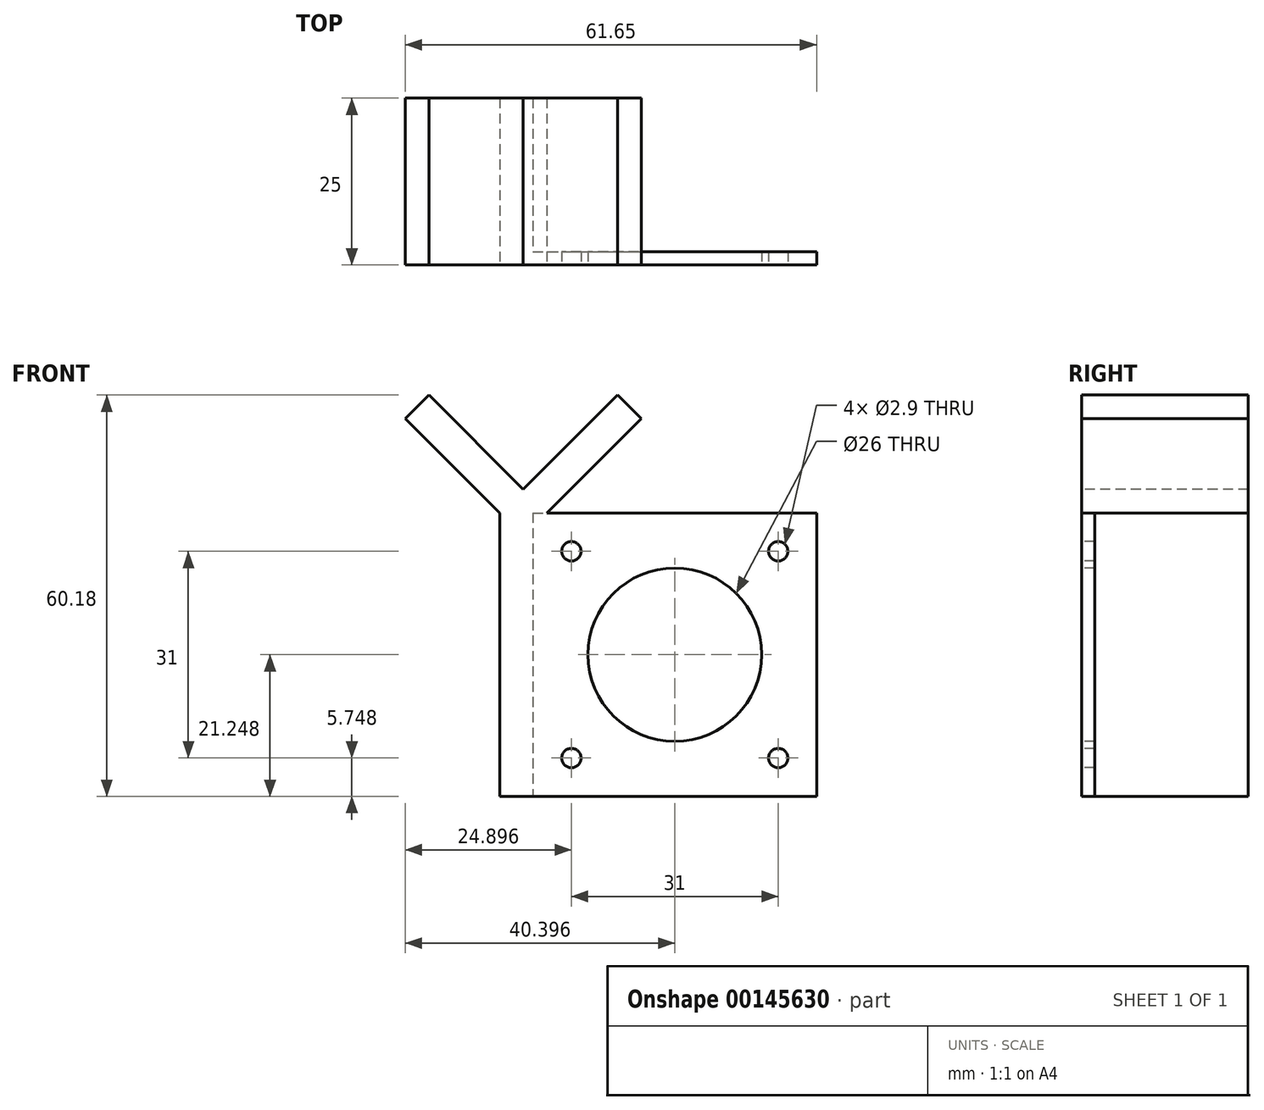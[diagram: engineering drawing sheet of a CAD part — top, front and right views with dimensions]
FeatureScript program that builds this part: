
annotation { "Feature Type Name" : "Feature", "Feature Type Description" : "" }
export const myFeature = defineFeature(function(context is Context, id is Id, definition is map)
    precondition{}
    {
        {
            var Q0;
            Q0=qCreatedBy(makeId("Front.planeOp"),FACE);
            var sketch = newSketch(context, id + "F0", { "sketchPlane" : qUnion([Q0])});
            skLineSegment(sketch, "E0.bottom", {"start": v(-36.86, -9.24) * mm, "end": v(-31.86, -9.24) * mm});
            skLineSegment(sketch, "E0.top", {"start": v(-36.86, -51.74) * mm, "end": v(-31.86, -51.74) * mm});
            skLineSegment(sketch, "E0.left", {"start": v(-36.86, -9.24) * mm, "end": v(-36.86, -51.74) * mm});
            skLineSegment(sketch, "E1.bottom", {"start": v(-31.86, -9.24) * mm, "end": v(10.64, -9.24) * mm});
            skLineSegment(sketch, "E1.top", {"start": v(-31.86, -51.74) * mm, "end": v(10.64, -51.74) * mm});
            skLineSegment(sketch, "E1.left", {"start": v(-31.86, -9.24) * mm, "end": v(-31.86, -51.74) * mm});
            skLineSegment(sketch, "E1.right", {"start": v(10.64, -9.24) * mm, "end": v(10.64, -51.74) * mm});
            skCircle(sketch, "E2", {"center": v(-26.11, -15) * mm, "radius": 1.45 * mm});
            skCircle(sketch, "E3", {"center": v(4.89, -15) * mm, "radius": 1.45 * mm});
            skCircle(sketch, "E4", {"center": v(-26.11, -46) * mm, "radius": 1.45 * mm});
            skCircle(sketch, "E5", {"center": v(4.89, -46) * mm, "radius": 1.45 * mm});
            skLineSegment(sketch, "E6", {"start": v(-29.8, -9.24) * mm, "end": v(-15.65, 4.9) * mm});
            skCircle(sketch, "E7", {"center": v(-10.61, -30.5) * mm, "radius": 13 * mm});
            skLineSegment(sketch, "E8", {"start": v(-47.47, 8.44) * mm, "end": v(-51, 4.9) * mm});
            skLineSegment(sketch, "E9", {"start": v(-51, 4.9) * mm, "end": v(-36.86, -9.24) * mm});
            skLineSegment(sketch, "E10", {"start": v(-15.65, 4.9) * mm, "end": v(-19.19, 8.44) * mm});
            skLineSegment(sketch, "E11", {"start": v(-19.19, 8.44) * mm, "end": v(-33.33, -5.7) * mm});
            skLineSegment(sketch, "E12", {"start": v(-47.47, 8.44) * mm, "end": v(-29.8, -9.24) * mm});
            skSolve(sketch);
        }
        {
            var Q0;
            Q0=makeQuery(id+"F0.imprint","IMPRINT",FACE,{"disambiguationData":[TD([[makeQuery(id+"F0.imprint","IMPRINT",EDGE,{"derivedFrom":sQuery(id+"F0.wireOp",EDGE,"NrFt3eKu-sJf2-EClc-BZI6-Y7PGvmtmYrN9")}),-1.0]])]});
            var Q1;
            Q1=makeQuery(id+"F0.imprint","IMPRINT",FACE,{"disambiguationData":[TD([[makeQuery(id+"F0.imprint","IMPRINT",EDGE,{"derivedFrom":sQuery(id+"F0.wireOp",EDGE,"E0.bottom")}),1.0]])]});
            var Q2;
            Q2=makeQuery(id+"F0.imprint","IMPRINT",FACE,{"disambiguationData":[TD([[makeQuery(id+"F0.imprint","IMPRINT",EDGE,{"derivedFrom":sQuery(id+"F0.wireOp",EDGE,"E0.bottom")}),-1.0]])]});
            var Q3;
            {var subQ0=sQuery(id+"F0.wireOp",EDGE,"RU0haTX9-gyN2-4ins-eghb-KWwRpY9zr3Yk");Q3=makeQuery(id+"F0.imprint","IMPRINT",FACE,{"disambiguationData":[TD([[makeQuery(id+"F0.imprint","IMPRINT",EDGE,{"derivedFrom":subQ0}),1.0]])]});}
            var Q4;
            {var subQ2=sQuery(id+"F0.wireOp",EDGE,"E6");Q4=makeQuery(id+"F0.imprint","IMPRINT",FACE,{"disambiguationData":[TD([[makeQuery(id+"F0.imprint","IMPRINT",EDGE,{"derivedFrom":subQ2}),-1.0]])]});}
            var Q5;
            {var subQ0=sQuery(id+"F0.wireOp",EDGE,"E6");Q5=makeQuery(id+"F0.imprint","IMPRINT",FACE,{"disambiguationData":[TD([[makeQuery(id+"F0.imprint","IMPRINT",EDGE,{"derivedFrom":subQ0}),1.0]])]});}
            extrude(context, id + "F1", {"entities" : qUnion([Q0, Q1, Q2, Q3, Q4, Q5]), "oppositeDirection" : true, "depth" : 25 * mm, "offsetDistance" : 25 * mm});
        }
        {
            var Q0;
            Q0=makeQuery(id+"F0.imprint","IMPRINT",FACE,{"disambiguationData":[TD([[makeQuery(id+"F0.imprint","IMPRINT",EDGE,{"derivedFrom":sQuery(id+"F0.wireOp",EDGE,"E1.bottom")}),-1.0]])]});
            extrude(context, id + "F2", {"entities" : qUnion([Q0]), "operationType" : NewBodyOperationType.ADD, "oppositeDirection" : true, "depth" : 2 * mm, "offsetDistance" : 25 * mm});
        }
        {
            var Q0;
            Q0=makeQuery(id+"F1.opExtrude","SWEPT_FACE",FACE,{"disambiguationData":[OSD([sQuery(id+"F0.wireOp",EDGE,"E12")])]});
            var sketch = newSketch(context, id + "F3", { "sketchPlane" : qUnion([Q0])});
            skCircle(sketch, "E13", {"center": v(-29.53, 12.5) * mm, "radius": 2 * mm});
            skSolve(sketch);
        }
        {
            var Q0;
            Q0=makeQuery(id+"F3.imprint","IMPRINT",FACE,{"disambiguationData":[TD([[makeQuery(id+"F3.imprint","IMPRINT",EDGE,{"derivedFrom":sQuery(id+"F3.wireOp",EDGE,"E13")}),1.0]])]});
            var Q1;
            Q1=makeQuery(id+"F3.imprint","IMPRINT",FACE,{"disambiguationData":[TD([[makeQuery(id+"F3.imprint","IMPRINT",EDGE,{"derivedFrom":sQuery(id+"F3.wireOp",EDGE,"bOpENU8F-jDej-Nupa-hcGo-BlWx3ok1s2gU")}),1.0]])]});
            extrude(context, id + "F4", {"entities" : qUnion([Q0, Q1]), "operationType" : NewBodyOperationType.REMOVE, "oppositeDirection" : true, "depth" : 25 * mm, "offsetDistance" : 25 * mm});
        }
    });
